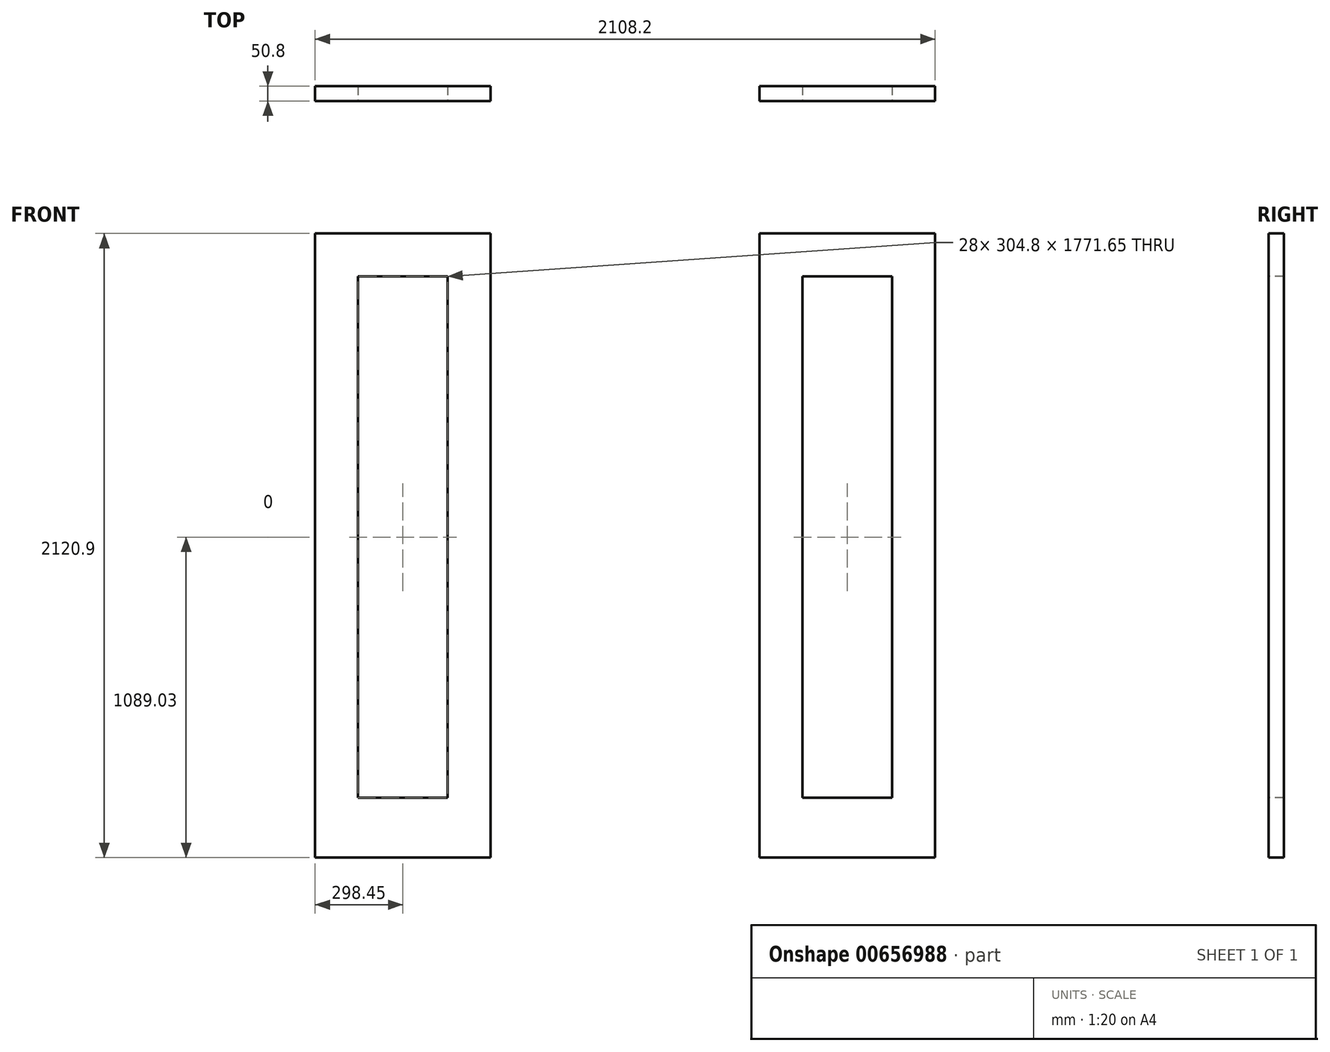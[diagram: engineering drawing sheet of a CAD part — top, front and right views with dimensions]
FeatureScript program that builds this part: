
annotation { "Feature Type Name" : "Feature", "Feature Type Description" : "" }
export const myFeature = defineFeature(function(context is Context, id is Id, definition is map)
    precondition{}
    {
        {
            var Q0;
            Q0=qCreatedBy(makeId("Front.planeOp"),FACE);
            var sketch = newSketch(context, id + "F0", { "sketchPlane" : qUnion([Q0])});
            skLineSegment(sketch, "E0.bottom", {"start": v(-1054.1, 1060.45) * mm, "end": v(1054.1, 1060.45) * mm});
            skLineSegment(sketch, "E0.top", {"start": v(-1054.1, -1060.45) * mm, "end": v(1054.1, -1060.45) * mm});
            skLineSegment(sketch, "E0.left", {"start": v(-1054.1, 1060.45) * mm, "end": v(-1054.1, -1060.45) * mm});
            skLineSegment(sketch, "E0.right", {"start": v(1054.1, 1060.45) * mm, "end": v(1054.1, -1060.45) * mm});
            skSolve(sketch);
        }
        {
            var Q0;
            Q0 = qSketchRegion(id + "F0", true);
            extrude(context, id + "F1", {"entities" : qUnion([Q0]), "depth" : 50.8 * mm, "offsetDistance" : 25.4 * mm});
        }
        {
            var Q0;
            Q0=makeQuery(id+"F1.opExtrude","CAP_FACE",FACE,{"disambiguationData":[OSD([sQuery(id+"F0.wireOp",EDGE,"E0.bottom"),sQuery(id+"F0.wireOp",EDGE,"E0.top"),sQuery(id+"F0.wireOp",EDGE,"E0.left"),sQuery(id+"F0.wireOp",EDGE,"E0.right")])],"isStart":false});
            var sketch = newSketch(context, id + "F2", { "sketchPlane" : qUnion([Q0])});
            skLineSegment(sketch, "E1.bottom", {"start": v(-457.2, 1060.45) * mm, "end": v(457.2, 1060.45) * mm});
            skLineSegment(sketch, "E1.top", {"start": v(-457.2, -1060.45) * mm, "end": v(457.2, -1060.45) * mm});
            skLineSegment(sketch, "E1.left", {"start": v(-457.2, 1060.45) * mm, "end": v(-457.2, -1060.45) * mm});
            skLineSegment(sketch, "E1.right", {"start": v(457.2, 1060.45) * mm, "end": v(457.2, -1060.45) * mm});
            skLineSegment(sketch, "E2", {"start": v(-457.2, 0) * mm, "end": v(-1054.1, 0) * mm, "construction": true});
            skLineSegment(sketch, "E3", {"start": v(457.2, 0) * mm, "end": v(1054.1, 0) * mm, "construction": true});
            skSolve(sketch);
        }
        {
            var Q0;
            Q0 = qSketchRegion(id + "F2", true);
            extrude(context, id + "F3", {"entities" : qUnion([Q0]), "operationType" : NewBodyOperationType.REMOVE, "oppositeDirection" : true, "depth" : 12.7 * mm, "offsetDistance" : 25.4 * mm});
        }
        {
            var Q0;
            Q0=makeQuery(id+"F3.boolean.opBoolean","COPY",FACE,{"derivedFrom":makeQuery(id+"F3.opExtrude","CAP_FACE",FACE,{"disambiguationData":[OSD([sQuery(id+"F2.wireOp",EDGE,"E1.bottom"),sQuery(id+"F2.wireOp",EDGE,"E1.top"),sQuery(id+"F2.wireOp",EDGE,"E1.left"),sQuery(id+"F2.wireOp",EDGE,"E1.right")])],"isStart":false})});
            var sketch = newSketch(context, id + "F4", { "sketchPlane" : qUnion([Q0])});
            skCircle(sketch, "E4", {"center": v(406.4, 0) * mm, "radius": 25.4 * mm});
            skSolve(sketch);
        }
        {
            var Q0;
            Q0 = qSketchRegion(id + "F4", true);
            extrude(context, id + "F5", {"entities" : qUnion([Q0]), "operationType" : NewBodyOperationType.REMOVE, "endBound" : BoundingType.THROUGH_ALL, "oppositeDirection" : true, "depth" : 25.4 * mm, "offsetDistance" : 25.4 * mm});
        }
        {
            var Q0;
            {var subQ0=sQuery(id+"F0.wireOp",EDGE,"E0.bottom");var subQ1=sQuery(id+"F0.wireOp",EDGE,"E0.top");var subQ2=sQuery(id+"F0.wireOp",EDGE,"E0.left");Q0=makeQuery(id+"F3.boolean.opBoolean","SPLIT",FACE,{"disambiguationData":[TD([makeQuery(id+"F1.opExtrude","SWEPT_FACE",FACE,{"disambiguationData":[OSD([subQ2])]})])],"derivedFrom":makeQuery(id+"F1.opExtrude","CAP_FACE",FACE,{"disambiguationData":[OSD([subQ0,subQ1,subQ2,sQuery(id+"F0.wireOp",EDGE,"E0.right")])],"isStart":false})});}
            var sketch = newSketch(context, id + "F6", { "sketchPlane" : qUnion([Q0])});
            skLineSegment(sketch, "E5.bottom", {"start": v(-908.05, 914.4) * mm, "end": v(-603.25, 914.4) * mm});
            skLineSegment(sketch, "E5.top", {"start": v(-908.05, -857.25) * mm, "end": v(-603.25, -857.25) * mm});
            skLineSegment(sketch, "E5.left", {"start": v(-908.05, 914.4) * mm, "end": v(-908.05, -857.25) * mm});
            skLineSegment(sketch, "E5.right", {"start": v(-603.25, 914.4) * mm, "end": v(-603.25, -857.25) * mm});
            skLineSegment(sketch, "E6.bottom", {"start": v(603.25, 914.4) * mm, "end": v(908.05, 914.4) * mm});
            skLineSegment(sketch, "E6.top", {"start": v(603.25, -857.25) * mm, "end": v(908.05, -857.25) * mm});
            skLineSegment(sketch, "E6.left", {"start": v(603.25, 914.4) * mm, "end": v(603.25, -857.25) * mm});
            skLineSegment(sketch, "E6.right", {"start": v(908.05, 914.4) * mm, "end": v(908.05, -857.25) * mm});
            skLineSegment(sketch, "E7", {"start": v(-908.05, 914.4) * mm, "end": v(-1054.1, 914.4) * mm, "construction": true});
            skLineSegment(sketch, "E8", {"start": v(908.05, 914.4) * mm, "end": v(1054.1, 914.4) * mm, "construction": true});
            skLineSegment(sketch, "E9", {"start": v(603.25, 914.4) * mm, "end": v(457.2, 914.4) * mm, "construction": true});
            skLineSegment(sketch, "E10", {"start": v(908.05, 914.4) * mm, "end": v(908.05, 1060.45) * mm, "construction": true});
            skSolve(sketch);
        }
        {
            var Q0;
            Q0 = qSketchRegion(id + "F6", true);
            extrude(context, id + "F7", {"entities" : qUnion([Q0]), "operationType" : NewBodyOperationType.REMOVE, "endBound" : BoundingType.THROUGH_ALL, "oppositeDirection" : true, "depth" : 25.4 * mm, "offsetDistance" : 25.4 * mm});
        }
        {
            var Q0;
            Q0 = qSketchRegion(id + "F2", true);
            extrude(context, id + "F8", {"entities" : qUnion([Q0]), "operationType" : NewBodyOperationType.REMOVE, "endBound" : BoundingType.THROUGH_ALL, "oppositeDirection" : true, "depth" : 25.4 * mm, "offsetDistance" : 25.4 * mm});
        }
    });
